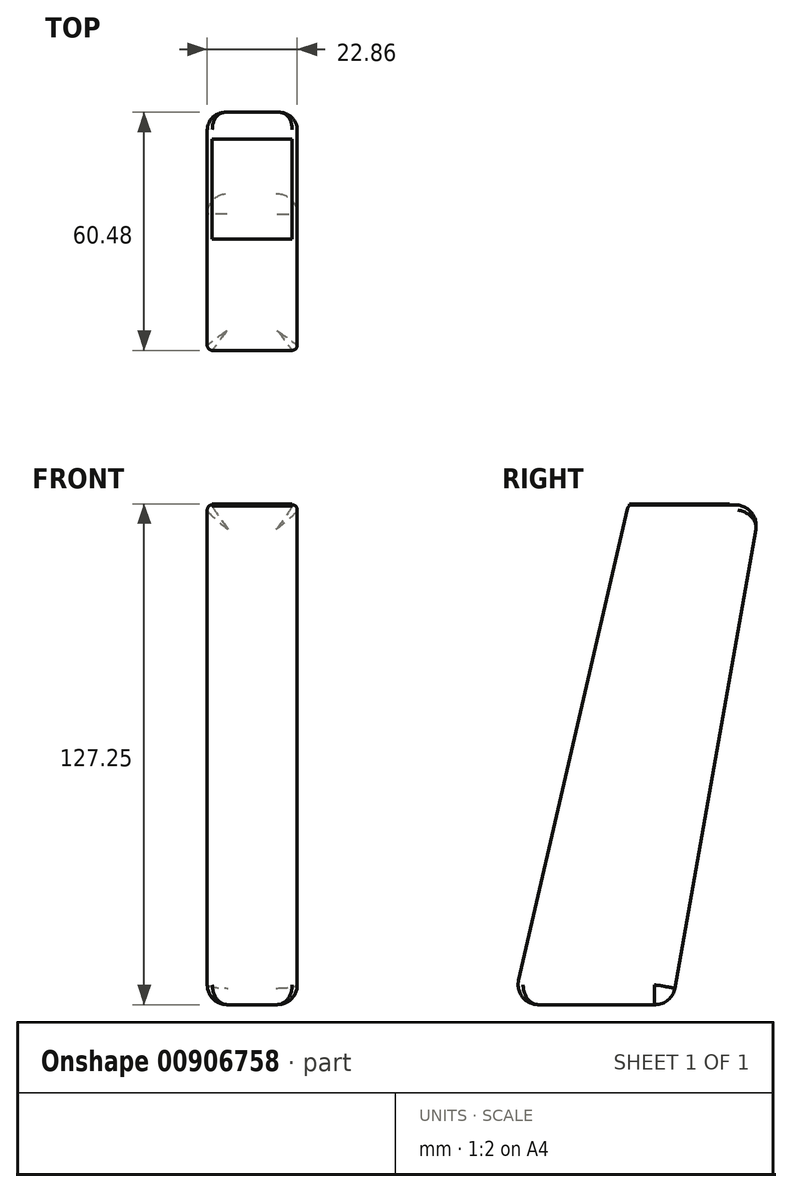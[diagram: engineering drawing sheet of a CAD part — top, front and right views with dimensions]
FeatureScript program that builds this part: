
annotation { "Feature Type Name" : "Feature", "Feature Type Description" : "" }
export const myFeature = defineFeature(function(context is Context, id is Id, definition is map)
    precondition{}
    {
        {
            var Q0;
            Q0=qCreatedBy(makeId("Top.planeOp"),FACE);
            var sketch = newSketch(context, id + "F0", { "sketchPlane" : qUnion([Q0])});
            skLineSegment(sketch, "E0.bottom", {"start": v(11.43, 31.75) * mm, "end": v(-11.43, 31.75) * mm});
            skLineSegment(sketch, "E0.top", {"start": v(11.43, -31.75) * mm, "end": v(-11.43, -31.75) * mm});
            skLineSegment(sketch, "E0.left", {"start": v(11.43, 31.75) * mm, "end": v(11.43, -31.75) * mm});
            skLineSegment(sketch, "E0.right", {"start": v(-11.43, 31.75) * mm, "end": v(-11.43, -31.75) * mm});
            skPoint(sketch, "E0.middle", {"position": v(0, 0) * mm});
            skSolve(sketch);
        }
        {
            var Q0;
            Q0 = qSketchRegion(id + "F0", true);
            extrude(context, id + "F1", {"entities" : qUnion([Q0]), "depth" : 127 * mm, "offsetDistance" : 25.4 * mm});
        }
        {
            var Q0;
            Q0=makeQuery(id+"F1.opExtrude","CAP_EDGE",EDGE,{"disambiguationData":[OSD([sQuery(id+"F0.wireOp",EDGE,"E0.bottom")])],"isStart":true});
            var Q1;
            Q1=makeQuery(id+"F1.opExtrude","CAP_EDGE",EDGE,{"disambiguationData":[OSD([sQuery(id+"F0.wireOp",EDGE,"E0.top")])],"isStart":false});
            chamfer(context, id + "F2", {"entities" : qUnion([Q0, Q1]), "chamferType" : ChamferType.OFFSET_ANGLE, "width" : 127 * mm, "oppositeDirection" : false, "angle" : 10 * degree, "tangentPropagation" : true});
        }
        {
            var Q0;
            Q0=makeQuery(id+"F1.opExtrude","CAP_FACE",FACE,{"disambiguationData":[OSD([sQuery(id+"F0.wireOp",EDGE,"E0.bottom"),sQuery(id+"F0.wireOp",EDGE,"E0.top"),sQuery(id+"F0.wireOp",EDGE,"E0.left"),sQuery(id+"F0.wireOp",EDGE,"E0.right")])],"isStart":false});
            var sketch = newSketch(context, id + "F3", { "sketchPlane" : qUnion([Q0])});
            skLineSegment(sketch, "E1.bottom", {"start": v(10.16, 23.9) * mm, "end": v(-10.16, 23.9) * mm});
            skLineSegment(sketch, "E1.top", {"start": v(10.16, -1.5) * mm, "end": v(-10.16, -1.5) * mm});
            skLineSegment(sketch, "E1.left", {"start": v(10.16, 23.9) * mm, "end": v(10.16, -1.5) * mm});
            skLineSegment(sketch, "E1.right", {"start": v(-10.16, 23.9) * mm, "end": v(-10.16, -1.5) * mm});
            skPoint(sketch, "E1.middle", {"position": v(0, 11.2) * mm});
            skPoint(sketch, "E1.middle.positionSnap0", {"position": v(0, 31.75) * mm});
            skPoint(sketch, "E1.middle.positionSnap1", {"position": v(-11.43, 11.2) * mm});
            skPoint(sketch, "E1.centerSnap0", {"position": v(0, 31.75) * mm});
            skPoint(sketch, "E1.centerSnap1", {"position": v(-11.43, 11.2) * mm});
            skSolve(sketch);
        }
        {
            var Q0;
            Q0=makeQuery(id+"F3.imprint","IMPRINT",FACE,{"disambiguationData":[TD([[makeQuery(id+"F3.imprint","IMPRINT",EDGE,{"derivedFrom":sQuery(id+"F3.wireOp",EDGE,"E1.bottom")}),1.0]])]});
            extrude(context, id + "F4", {"entities" : qUnion([Q0]), "operationType" : NewBodyOperationType.ADD, "depth" : 0.25 * mm, "offsetDistance" : 25.4 * mm});
        }
        {
            var Q0;
            {var subQ0=sQuery(id+"F0.wireOp",EDGE,"E0.top");Q0=makeQuery(id+"F2.opChamfer","BLEND_EDGE",EDGE,{"blendedFrom":[makeQuery(id+"F1.opExtrude","CAP_EDGE",EDGE,{"disambiguationData":[OSD([subQ0])],"isStart":false}),makeQuery(id+"F1.opExtrude","CAP_FACE",FACE,{"disambiguationData":[OSD([sQuery(id+"F0.wireOp",EDGE,"E0.bottom"),subQ0,sQuery(id+"F0.wireOp",EDGE,"E0.left"),sQuery(id+"F0.wireOp",EDGE,"E0.right")])],"isStart":false})],"blendedInto":[makeQuery(id+"F1.opExtrude","CAP_FACE",FACE,{"disambiguationData":[OSD([sQuery(id+"F0.wireOp",EDGE,"E0.bottom"),subQ0,sQuery(id+"F0.wireOp",EDGE,"E0.left"),sQuery(id+"F0.wireOp",EDGE,"E0.right")])],"isStart":false})]});}
            chamfer(context, id + "F5", {"entities" : qUnion([Q0]), "chamferType" : ChamferType.OFFSET_ANGLE, "width" : 7.62 * mm, "oppositeDirection" : false, "angle" : 77 * degree, "tangentPropagation" : true});
        }
        {
            var Q0;
            {var subQ0=sQuery(id+"F0.wireOp",EDGE,"E0.right");var subQ1=sQuery(id+"F0.wireOp",EDGE,"E0.top");Q0=makeQuery(id+"F5.opChamfer","BLEND_EDGE",EDGE,{"blendedFrom":[makeQuery(id+"F2.opChamfer","BLEND_EDGE",EDGE,{"blendedFrom":[makeQuery(id+"F1.opExtrude","CAP_EDGE",EDGE,{"disambiguationData":[OSD([subQ1])],"isStart":false}),makeQuery(id+"F1.opExtrude","CAP_FACE",FACE,{"disambiguationData":[OSD([sQuery(id+"F0.wireOp",EDGE,"E0.bottom"),subQ1,sQuery(id+"F0.wireOp",EDGE,"E0.left"),subQ0])],"isStart":false})],"blendedInto":[makeQuery(id+"F1.opExtrude","CAP_FACE",FACE,{"disambiguationData":[OSD([sQuery(id+"F0.wireOp",EDGE,"E0.bottom"),subQ1,sQuery(id+"F0.wireOp",EDGE,"E0.left"),subQ0])],"isStart":false})]}),makeQuery(id+"F1.opExtrude","SWEPT_FACE",FACE,{"disambiguationData":[OSD([subQ0])]})],"blendedInto":[makeQuery(id+"F1.opExtrude","SWEPT_FACE",FACE,{"disambiguationData":[OSD([subQ0])]})]});}
            var Q1;
            {var subQ0=sQuery(id+"F0.wireOp",EDGE,"E0.left");var subQ1=sQuery(id+"F0.wireOp",EDGE,"E0.top");Q1=makeQuery(id+"F5.opChamfer","BLEND_EDGE",EDGE,{"blendedFrom":[makeQuery(id+"F2.opChamfer","BLEND_EDGE",EDGE,{"blendedFrom":[makeQuery(id+"F1.opExtrude","CAP_EDGE",EDGE,{"disambiguationData":[OSD([subQ1])],"isStart":false}),makeQuery(id+"F1.opExtrude","CAP_FACE",FACE,{"disambiguationData":[OSD([sQuery(id+"F0.wireOp",EDGE,"E0.bottom"),subQ1,subQ0,sQuery(id+"F0.wireOp",EDGE,"E0.right")])],"isStart":false})],"blendedInto":[makeQuery(id+"F1.opExtrude","CAP_FACE",FACE,{"disambiguationData":[OSD([sQuery(id+"F0.wireOp",EDGE,"E0.bottom"),subQ1,subQ0,sQuery(id+"F0.wireOp",EDGE,"E0.right")])],"isStart":false})]}),makeQuery(id+"F1.opExtrude","SWEPT_FACE",FACE,{"disambiguationData":[OSD([subQ0])]})],"blendedInto":[makeQuery(id+"F1.opExtrude","SWEPT_FACE",FACE,{"disambiguationData":[OSD([subQ0])]})]});}
            fillet(context, id + "F6", {"entities" : qUnion([Q0, Q1]), "radius" : 1.27 * mm, "tangentPropagation" : true, "allowEdgeOverflow" : false});
        }
        {
            var Q0;
            Q0=makeQuery(id+"F1.opExtrude","CAP_EDGE",EDGE,{"disambiguationData":[OSD([sQuery(id+"F0.wireOp",EDGE,"E0.right")])],"isStart":false});
            var Q1;
            Q1=makeQuery(id+"F1.opExtrude","CAP_EDGE",EDGE,{"disambiguationData":[OSD([sQuery(id+"F0.wireOp",EDGE,"E0.left")])],"isStart":false});
            fillet(context, id + "F7", {"entities" : qUnion([Q0, Q1]), "radius" : 1.27 * mm, "tangentPropagation" : true, "allowEdgeOverflow" : false});
        }
        {
            var Q0;
            {var subQ0=sQuery(id+"F0.wireOp",EDGE,"E0.bottom");Q0=makeQuery(id+"F2.opChamfer","BLEND_EDGE",EDGE,{"blendedFrom":[makeQuery(id+"F1.opExtrude","CAP_EDGE",EDGE,{"disambiguationData":[OSD([subQ0])],"isStart":true}),makeQuery(id+"F1.opExtrude","CAP_FACE",FACE,{"disambiguationData":[OSD([subQ0,sQuery(id+"F0.wireOp",EDGE,"E0.top"),sQuery(id+"F0.wireOp",EDGE,"E0.left"),sQuery(id+"F0.wireOp",EDGE,"E0.right")])],"isStart":false})],"blendedInto":[makeQuery(id+"F1.opExtrude","CAP_FACE",FACE,{"disambiguationData":[OSD([subQ0,sQuery(id+"F0.wireOp",EDGE,"E0.top"),sQuery(id+"F0.wireOp",EDGE,"E0.left"),sQuery(id+"F0.wireOp",EDGE,"E0.right")])],"isStart":false})]});}
            fillet(context, id + "F8", {"entities" : qUnion([Q0]), "radius" : 5.33 * mm, "tangentPropagation" : true, "allowEdgeOverflow" : false});
        }
        {
            var Q0;
            Q0=makeQuery(id+"F1.opExtrude","CAP_FACE",FACE,{"disambiguationData":[OSD([sQuery(id+"F0.wireOp",EDGE,"E0.bottom"),sQuery(id+"F0.wireOp",EDGE,"E0.top"),sQuery(id+"F0.wireOp",EDGE,"E0.left"),sQuery(id+"F0.wireOp",EDGE,"E0.right")])],"isStart":true});
            fillet(context, id + "F9", {"entities" : qUnion([Q0]), "radius" : 5.08 * mm, "tangentPropagation" : true, "allowEdgeOverflow" : false});
        }
    });
